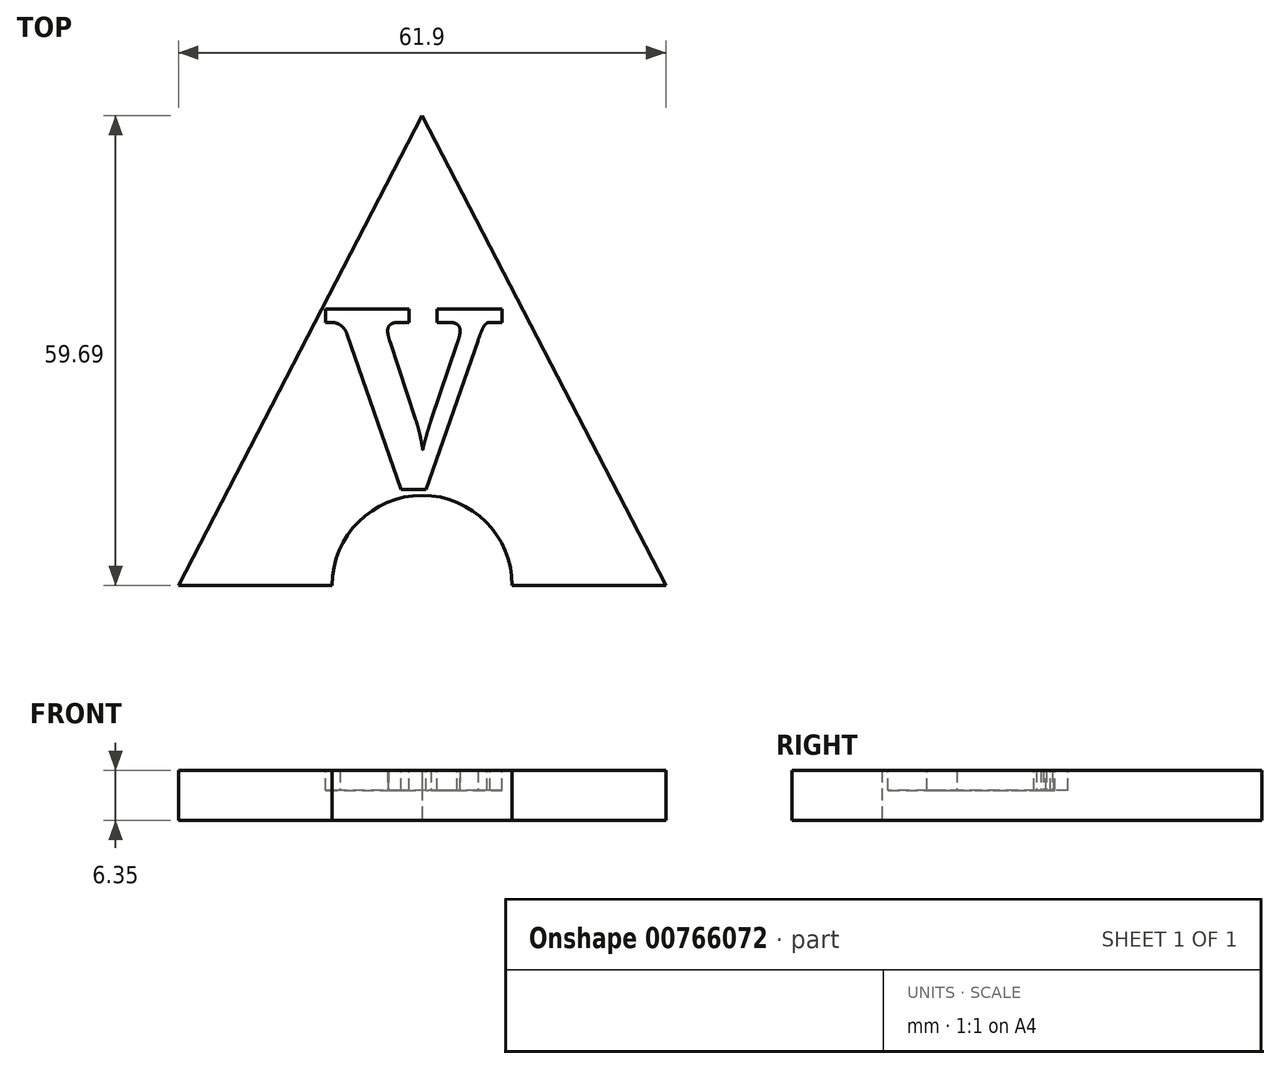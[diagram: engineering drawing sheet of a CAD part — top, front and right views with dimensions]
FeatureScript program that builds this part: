
annotation { "Feature Type Name" : "Feature", "Feature Type Description" : "" }
export const myFeature = defineFeature(function(context is Context, id is Id, definition is map)
    precondition{}
    {
        {
            var Q0;
            Q0=qCreatedBy(makeId("Top.planeOp"),FACE);
            var sketch = newSketch(context, id + "F0", { "sketchPlane" : qUnion([Q0])});
            skCircle(sketch, "E0.cCircle", {"center": v(0, 0) * mm, "radius": 16.2 * mm, "construction": true});
            skLineSegment(sketch, "E0.0", {"start": v(30.95, -16.2) * mm, "end": v(-30.95, -16.2) * mm});
            skLineSegment(sketch, "E0.1", {"start": v(-30.95, -16.2) * mm, "end": v(0, 43.48) * mm});
            skLineSegment(sketch, "E0.2", {"start": v(0, 43.48) * mm, "end": v(30.95, -16.2) * mm});
            skPoint(sketch, "E0.0.midPoint", {"position": v(0, -16.2) * mm});
            skSolve(sketch);
        }
        {
            var Q0;
            Q0=makeQuery(id+"F0.imprint","IMPRINT",FACE,{"disambiguationData":[TD([[makeQuery(id+"F0.imprint","IMPRINT",EDGE,{"derivedFrom":sQuery(id+"F0.wireOp",EDGE,"E0.0")}),-1.0]])]});
            extrude(context, id + "F1", {"entities" : qUnion([Q0]), "depth" : 6.35 * mm, "offsetDistance" : 25.4 * mm});
        }
        {
            var Q0;
            Q0=sQuery(id+"F0.wireOp",VERTEX,"E0.0.midPoint");
            var Q1;
            Q1=makeQuery(id+"F1.opExtrude","SWEPT_BODY",BODY,{"disambiguationData":[OSD([sQuery(id+"F0.wireOp",EDGE,"E0.0"),sQuery(id+"F0.wireOp",EDGE,"E0.1"),sQuery(id+"F0.wireOp",EDGE,"E0.2")])]});
            hole(context, id + "F2", {"style" : HoleStyle.SIMPLE, "endStyle" : HoleEndStyle.THROUGH, "oppositeDirection" : true, "holeDiameter" : 22.86 * mm, "majorDiameter" : 6.35 * mm, "isTappedThrough" : true, "tappedDepth" : 12.7 * mm, "tapClearance" : 3, "locations" : qUnion([Q0]), "scope" : qUnion([Q1])});
        }
        {
            var Q0;
            Q0=makeQuery(id+"F1.opExtrude","CAP_FACE",FACE,{"disambiguationData":[OSD([sQuery(id+"F0.wireOp",EDGE,"E0.0"),sQuery(id+"F0.wireOp",EDGE,"E0.1"),sQuery(id+"F0.wireOp",EDGE,"E0.2")])],"isStart":false});
            var sketch = newSketch(context, id + "F3", { "sketchPlane" : qUnion([Q0])});
            skText(sketch, "E1", { "text": "V", "fontName": "NotoSerif-Bold.ttf"});
            const initialGuessF3  = {"E1": [-0.01225, -0.00402, 1, 0, 0.02311]};
            skSetInitialGuess(sketch, initialGuessF3);
            skSolve(sketch);
        }
        {
            var Q0;
            Q0 = qSketchRegion(id + "F3", true);
            extrude(context, id + "F4", {"entities" : qUnion([Q0]), "operationType" : NewBodyOperationType.REMOVE, "oppositeDirection" : true, "depth" : 2.54 * mm, "offsetDistance" : 25.4 * mm});
        }
    });
